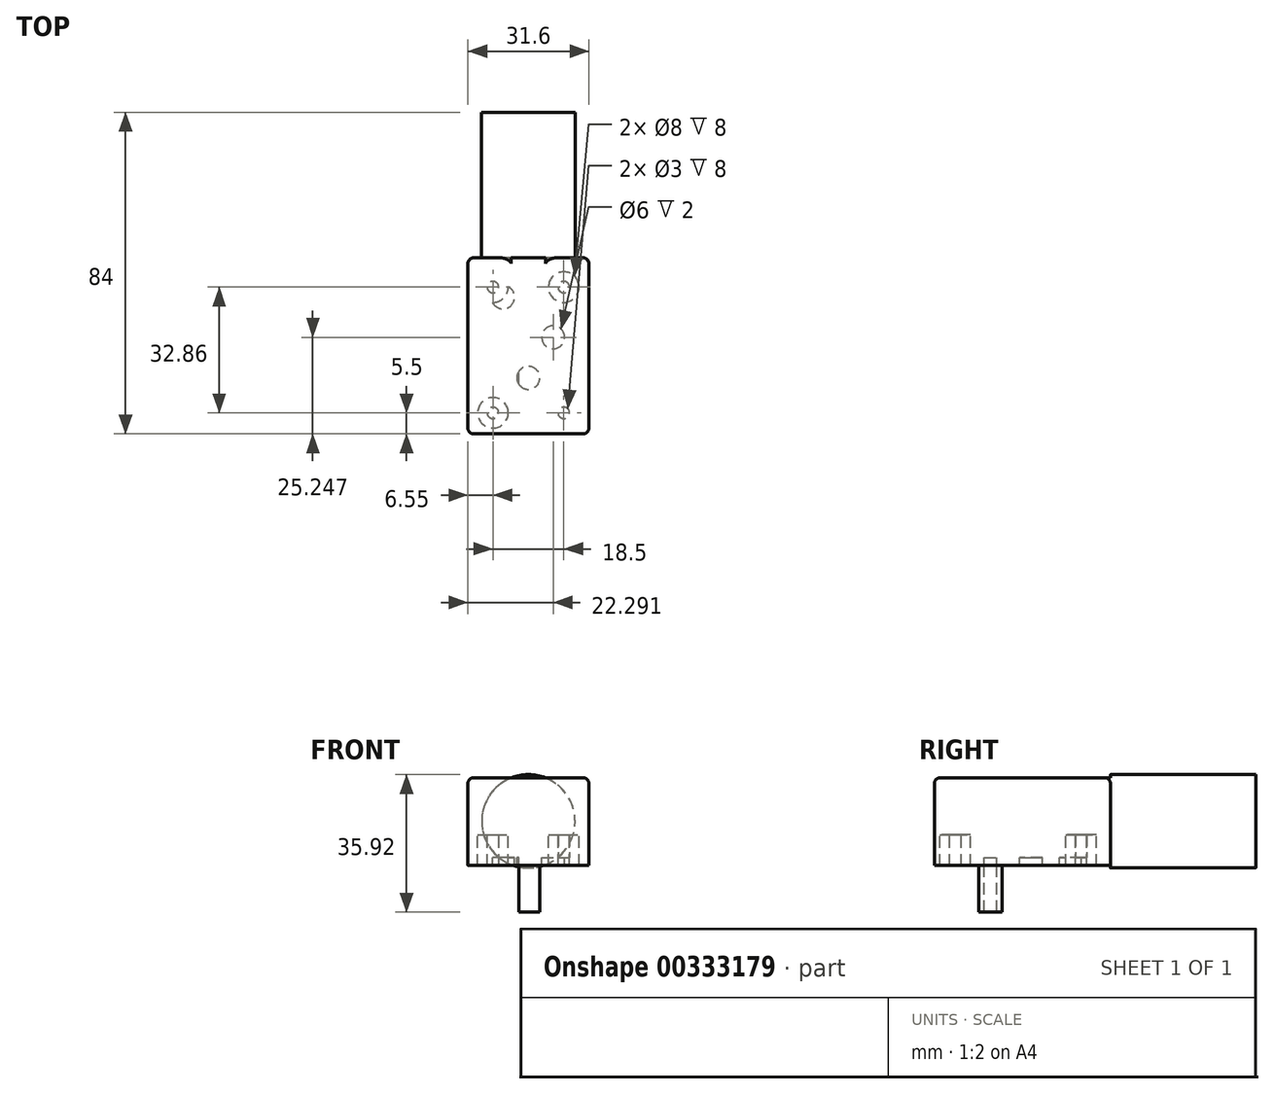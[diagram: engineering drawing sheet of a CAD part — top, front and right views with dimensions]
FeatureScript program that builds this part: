
annotation { "Feature Type Name" : "Feature", "Feature Type Description" : "" }
export const myFeature = defineFeature(function(context is Context, id is Id, definition is map)
    precondition{}
    {
        {
            var Q0;
            Q0=qCreatedBy(makeId("Top.planeOp"),FACE);
            var sketch = newSketch(context, id + "F0", { "sketchPlane" : qUnion([Q0])});
            skLineSegment(sketch, "E0.bottom", {"start": v(15.8, 23) * mm, "end": v(-15.8, 23) * mm});
            skLineSegment(sketch, "E0.top", {"start": v(15.8, -23) * mm, "end": v(-15.8, -23) * mm});
            skLineSegment(sketch, "E0.left", {"start": v(15.8, 23) * mm, "end": v(15.8, -23) * mm});
            skLineSegment(sketch, "E0.right", {"start": v(-15.8, 23) * mm, "end": v(-15.8, -23) * mm});
            skPoint(sketch, "E0.middle", {"position": v(0, 0) * mm});
            skSolve(sketch);
        }
        {
            var Q0;
            Q0=qSketchRegion(id+"F0",true);
            extrude(context, id + "F1", {"entities" : qUnion([Q0]), "depth" : 20.9 * mm});
        }
        {
            var Q0;
            Q0=makeQuery(id+"F1.opExtrude","SWEPT_FACE",FACE,{"disambiguationData":[OSD([sQuery(id+"F0.wireOp",EDGE,"E0.bottom")])]});
            var sketch = newSketch(context, id + "F2", { "sketchPlane" : qUnion([Q0])});
            skCircle(sketch, "E1", {"center": v(0, 9.55) * mm, "radius": 12.2 * mm});
            skSolve(sketch);
        }
        {
            var Q0;
            Q0=qSketchRegion(id+"F2",true);
            extrude(context, id + "F3", {"entities" : qUnion([Q0]), "operationType" : NewBodyOperationType.ADD, "depth" : 38 * mm});
        }
        {
            var Q0;
            Q0=makeQuery(id+"F1.opExtrude","CAP_FACE",FACE,{"disambiguationData":[OSD([sQuery(id+"F0.wireOp",EDGE,"E0.bottom"),sQuery(id+"F0.wireOp",EDGE,"E0.top"),sQuery(id+"F0.wireOp",EDGE,"E0.left"),sQuery(id+"F0.wireOp",EDGE,"E0.right")])],"isStart":true});
            var sketch = newSketch(context, id + "F4", { "sketchPlane" : qUnion([Q0])});
            skCircle(sketch, "E2", {"center": v(0, 8.35) * mm, "radius": 3 * mm});
            skCircle(sketch, "E3", {"center": v(0, 8.35) * mm, "radius": 7.23 * mm});
            skLineSegment(sketch, "E4", {"start": v(3, 8.35) * mm, "end": v(-2.5, 8.35) * mm});
            skLineSegment(sketch, "E5", {"start": v(-2.5, 10) * mm, "end": v(-2.5, 6.7) * mm});
            skCircle(sketch, "E6", {"center": v(9.25, 17.5) * mm, "radius": 4 * mm});
            skCircle(sketch, "E7", {"center": v(9.25, 17.5) * mm, "radius": 1.5 * mm});
            skLineSegment(sketch, "E8", {"start": v(0, 23) * mm, "end": v(0, 18.4) * mm});
            skPoint(sketch, "E8.endSnap0", {"position": v(0, 23) * mm});
            skCircle(sketch, "E9.MirrorC", {"center": v(-9.25, 17.5) * mm, "radius": 1.5 * mm});
            skCircle(sketch, "E10.MirrorC", {"center": v(-9.25, 17.5) * mm, "radius": 4 * mm});
            skCircle(sketch, "E11", {"center": v(-6.5, -2.25) * mm, "radius": 3 * mm});
            skCircle(sketch, "E12.MirrorC", {"center": v(6.5, -2.25) * mm, "radius": 3 * mm});
            skCircle(sketch, "E13", {"center": v(-9.25, -15.36) * mm, "radius": 4 * mm});
            skCircle(sketch, "E14.MirrorC", {"center": v(9.25, -15.36) * mm, "radius": 4 * mm});
            skCircle(sketch, "E15", {"center": v(-9.25, -15.36) * mm, "radius": 1.5 * mm});
            skCircle(sketch, "E16.MirrorC", {"center": v(9.25, -15.36) * mm, "radius": 1.5 * mm});
            skCircle(sketch, "E17", {"center": v(-6.67, -12.72) * mm, "radius": 3.05 * mm});
            skSolve(sketch);
        }
        {
            var Q0;
            Q0=makeQuery(id+"F4.imprint","IMPRINT",FACE,{"disambiguationData":[TD([[makeQuery(id+"F4.imprint","IMPRINT",EDGE,{"derivedFrom":sQuery(id+"F4.wireOp",EDGE,"E3")}),1.0]])]});
            var Q1;
            Q1=makeQuery(id+"F4.imprint","IMPRINT",FACE,{"disambiguationData":[TD([[makeQuery(id+"F4.imprint","IMPRINT",EDGE,{"derivedFrom":sQuery(id+"F4.wireOp",EDGE,"E6")}),1.0]])]});
            var Q2;
            Q2=makeQuery(id+"F4.imprint","IMPRINT",FACE,{"disambiguationData":[TD([[makeQuery(id+"F4.imprint","IMPRINT",EDGE,{"derivedFrom":sQuery(id+"F4.wireOp",EDGE,"E9.MirrorC")}),1.0]])]});
            var Q3;
            Q3=makeQuery(id+"F4.imprint","IMPRINT",FACE,{"disambiguationData":[TD([[makeQuery(id+"F4.imprint","IMPRINT",EDGE,{"derivedFrom":sQuery(id+"F4.wireOp",EDGE,"E11")}),1.0]])]});
            var Q4;
            Q4=makeQuery(id+"F4.imprint","IMPRINT",FACE,{"disambiguationData":[TD([[makeQuery(id+"F4.imprint","IMPRINT",EDGE,{"derivedFrom":sQuery(id+"F4.wireOp",EDGE,"E12.MirrorC")}),-1.0]])]});
            var Q5;
            Q5=makeQuery(id+"F4.imprint","IMPRINT",FACE,{"disambiguationData":[TD([[makeQuery(id+"F4.imprint","IMPRINT",EDGE,{"derivedFrom":sQuery(id+"F4.wireOp",EDGE,"E14.MirrorC")}),-1.0]])]});
            var Q6;
            {var subQ0=sQuery(id+"F4.wireOp",EDGE,"NOkgakyG-LXeg-HDE5-BnBK-bHET0c2Zb8rj");var subQ1=sQuery(id+"F4.wireOp",EDGE,"E13");var subQ2=makeQuery(id+"F4.imprint","INTERSECT",VERTEX,{"disambiguationData":[OD(0.0)],"derivedFrom":[subQ1,subQ0]});Q6=makeQuery(id+"F4.imprint","IMPRINT",FACE,{"disambiguationData":[TD([[makeQuery(id+"F4.imprint","IMPRINT",EDGE,{"disambiguationData":[TD([[subQ2,1.0]])],"derivedFrom":subQ1}),-1.0]])]});}
            var Q7;
            Q7=makeQuery(id+"F4.imprint","IMPRINT",FACE,{"disambiguationData":[TD([[makeQuery(id+"F4.imprint","IMPRINT",EDGE,{"derivedFrom":sQuery(id+"F4.wireOp",EDGE,"E15")}),-1.0]])]});
            var Q8;
            {var subQ0=sQuery(id+"F4.wireOp",EDGE,"E17");var subQ1=sQuery(id+"F4.wireOp",EDGE,"E13");var subQ2=makeQuery(id+"F4.imprint","INTERSECT",VERTEX,{"disambiguationData":[OD(0.0)],"derivedFrom":[subQ1,subQ0]});Q8=makeQuery(id+"F4.imprint","IMPRINT",FACE,{"disambiguationData":[TD([[makeQuery(id+"F4.imprint","IMPRINT",EDGE,{"disambiguationData":[TD([[subQ2,1.0]])],"derivedFrom":subQ1}),1.0]])]});}
            var Q9;
            {var subQ0=sQuery(id+"F4.wireOp",EDGE,"E5");var subQ1=sQuery(id+"F4.wireOp",EDGE,"E2");var subQ2=makeQuery(id+"F4.imprint","INTERSECT",VERTEX,{"disambiguationData":[OD(0.0)],"derivedFrom":[subQ1,subQ0]});Q9=makeQuery(id+"F4.imprint","IMPRINT",FACE,{"disambiguationData":[TD([[makeQuery(id+"F4.imprint","IMPRINT",EDGE,{"disambiguationData":[TD([[subQ2,-1.0]])],"derivedFrom":subQ1}),1.0]])]});}
            extrude(context, id + "F5", {"entities" : qUnion([Q0, Q1, Q2, Q3, Q4, Q5, Q6, Q7, Q8, Q9]), "operationType" : NewBodyOperationType.ADD, "depth" : 2 * mm});
        }
        {
            var Q0;
            {var subQ0=sQuery(id+"F4.wireOp",EDGE,"E4");Q0=makeQuery(id+"F4.imprint","IMPRINT",FACE,{"disambiguationData":[TD([[makeQuery(id+"F4.imprint","IMPRINT",EDGE,{"derivedFrom":subQ0}),-1.0]])]});}
            var Q1;
            {var subQ0=sQuery(id+"F4.wireOp",EDGE,"E4");Q1=makeQuery(id+"F4.imprint","IMPRINT",FACE,{"disambiguationData":[TD([[makeQuery(id+"F4.imprint","IMPRINT",EDGE,{"derivedFrom":subQ0}),1.0]])]});}
            extrude(context, id + "F6", {"entities" : qUnion([Q0, Q1]), "operationType" : NewBodyOperationType.ADD, "depth" : 14.17 * mm});
        }
        {
            var Q0;
            {var subQ0=sQuery(id+"F4.wireOp",EDGE,"E17");var subQ1=sQuery(id+"F4.wireOp",EDGE,"E15");var subQ2=makeQuery(id+"F4.imprint","INTERSECT",VERTEX,{"disambiguationData":[OD(0.0)],"derivedFrom":[subQ1,subQ0]});Q0=makeQuery(id+"F4.imprint","IMPRINT",FACE,{"disambiguationData":[TD([[makeQuery(id+"F4.imprint","IMPRINT",EDGE,{"disambiguationData":[TD([[subQ2,1.0]])],"derivedFrom":subQ1}),1.0]])]});}
            var Q1;
            Q1=makeQuery(id+"F4.imprint","IMPRINT",FACE,{"disambiguationData":[TD([[makeQuery(id+"F4.imprint","IMPRINT",EDGE,{"derivedFrom":sQuery(id+"F4.wireOp",EDGE,"E16.MirrorC")}),-1.0]])]});
            var Q2;
            Q2=makeQuery(id+"F4.imprint","IMPRINT",FACE,{"disambiguationData":[TD([[makeQuery(id+"F4.imprint","IMPRINT",EDGE,{"derivedFrom":sQuery(id+"F4.wireOp",EDGE,"E7")}),1.0]])]});
            var Q3;
            Q3=makeQuery(id+"F4.imprint","IMPRINT",FACE,{"disambiguationData":[TD([[makeQuery(id+"F4.imprint","IMPRINT",EDGE,{"derivedFrom":sQuery(id+"F4.wireOp",EDGE,"E9.MirrorC")}),-1.0]])]});
            var Q4;
            {var subQ0=sQuery(id+"F4.wireOp",EDGE,"E17");var subQ1=sQuery(id+"F4.wireOp",EDGE,"E15");var subQ2=makeQuery(id+"F4.imprint","INTERSECT",VERTEX,{"disambiguationData":[OD(0.0)],"derivedFrom":[subQ1,subQ0]});Q4=makeQuery(id+"F4.imprint","IMPRINT",FACE,{"disambiguationData":[TD([[makeQuery(id+"F4.imprint","IMPRINT",EDGE,{"disambiguationData":[TD([[subQ2,-1.0]])],"derivedFrom":subQ1}),1.0]])]});}
            extrude(context, id + "F7", {"entities" : qUnion([Q0, Q1, Q2, Q3, Q4]), "operationType" : NewBodyOperationType.REMOVE, "oppositeDirection" : true, "depth" : 6 * mm});
        }
        {
            var Q0;
            Q0=makeQuery(id+"F1.opExtrude","CAP_EDGE",EDGE,{"disambiguationData":[OSD([sQuery(id+"F0.wireOp",EDGE,"E0.left")])],"isStart":false});
            var Q1;
            Q1=makeQuery(id+"F1.opExtrude","SWEPT_EDGE",EDGE,{"disambiguationData":[OSD([sQuery(id+"F0.wireOp",EDGE,"E0.bottom"),sQuery(id+"F0.wireOp",EDGE,"E0.left")])]});
            var Q2;
            {var subQ1=sQuery(id+"F0.wireOp",EDGE,"E0.left");var subQ2=sQuery(id+"F0.wireOp",EDGE,"E0.bottom");var subQ3=makeQuery(id+"F1.opExtrude","CAP_FACE",FACE,{"disambiguationData":[OSD([subQ2,sQuery(id+"F0.wireOp",EDGE,"E0.top"),subQ1,sQuery(id+"F0.wireOp",EDGE,"E0.right")])],"isStart":false});var subQ4=makeQuery(id+"F1.opExtrude","SWEPT_FACE",FACE,{"disambiguationData":[OSD([subQ2])]});Q2=makeQuery(id+"F3.boolean.opBoolean","SPLIT",EDGE,{"disambiguationData":[topologyDisambiguationEdgeConnected([subQ4,subQ3]),TD([makeQuery(id+"F1.opExtrude","SWEPT_FACE",FACE,{"disambiguationData":[OSD([subQ1])]})])],"derivedFrom":makeQuery(id+"F1.opExtrude","CAP_EDGE",EDGE,{"disambiguationData":[OSD([subQ2])],"isStart":false})});}
            var Q3;
            {var subQ1=sQuery(id+"F0.wireOp",EDGE,"E0.right");var subQ2=sQuery(id+"F0.wireOp",EDGE,"E0.bottom");var subQ3=makeQuery(id+"F1.opExtrude","CAP_FACE",FACE,{"disambiguationData":[OSD([subQ2,sQuery(id+"F0.wireOp",EDGE,"E0.top"),sQuery(id+"F0.wireOp",EDGE,"E0.left"),subQ1])],"isStart":false});var subQ4=makeQuery(id+"F1.opExtrude","SWEPT_FACE",FACE,{"disambiguationData":[OSD([subQ2])]});Q3=makeQuery(id+"F3.boolean.opBoolean","SPLIT",EDGE,{"disambiguationData":[topologyDisambiguationEdgeConnected([subQ4,subQ3]),TD([makeQuery(id+"F1.opExtrude","SWEPT_FACE",FACE,{"disambiguationData":[OSD([subQ1])]})])],"derivedFrom":makeQuery(id+"F1.opExtrude","CAP_EDGE",EDGE,{"disambiguationData":[OSD([subQ2])],"isStart":false})});}
            var Q4;
            Q4=makeQuery(id+"F1.opExtrude","CAP_EDGE",EDGE,{"disambiguationData":[OSD([sQuery(id+"F0.wireOp",EDGE,"E0.right")])],"isStart":false});
            var Q5;
            Q5=makeQuery(id+"F1.opExtrude","SWEPT_EDGE",EDGE,{"disambiguationData":[OSD([sQuery(id+"F0.wireOp",EDGE,"E0.bottom"),sQuery(id+"F0.wireOp",EDGE,"E0.right")])]});
            var Q6;
            Q6=makeQuery(id+"F1.opExtrude","SWEPT_EDGE",EDGE,{"disambiguationData":[OSD([sQuery(id+"F0.wireOp",EDGE,"E0.top"),sQuery(id+"F0.wireOp",EDGE,"E0.right")])]});
            var Q7;
            Q7=makeQuery(id+"F1.opExtrude","CAP_EDGE",EDGE,{"disambiguationData":[OSD([sQuery(id+"F0.wireOp",EDGE,"E0.top")])],"isStart":false});
            var Q8;
            Q8=makeQuery(id+"F1.opExtrude","SWEPT_EDGE",EDGE,{"disambiguationData":[OSD([sQuery(id+"F0.wireOp",EDGE,"E0.top"),sQuery(id+"F0.wireOp",EDGE,"E0.left")])]});
            fillet(context, id + "F8", {"entities" : qUnion([Q0, Q1, Q2, Q3, Q4, Q5, Q6, Q7, Q8]), "radius" : 1.5 * mm, "tangentPropagation" : true, "allowEdgeOverflow" : false});
        }
    });
